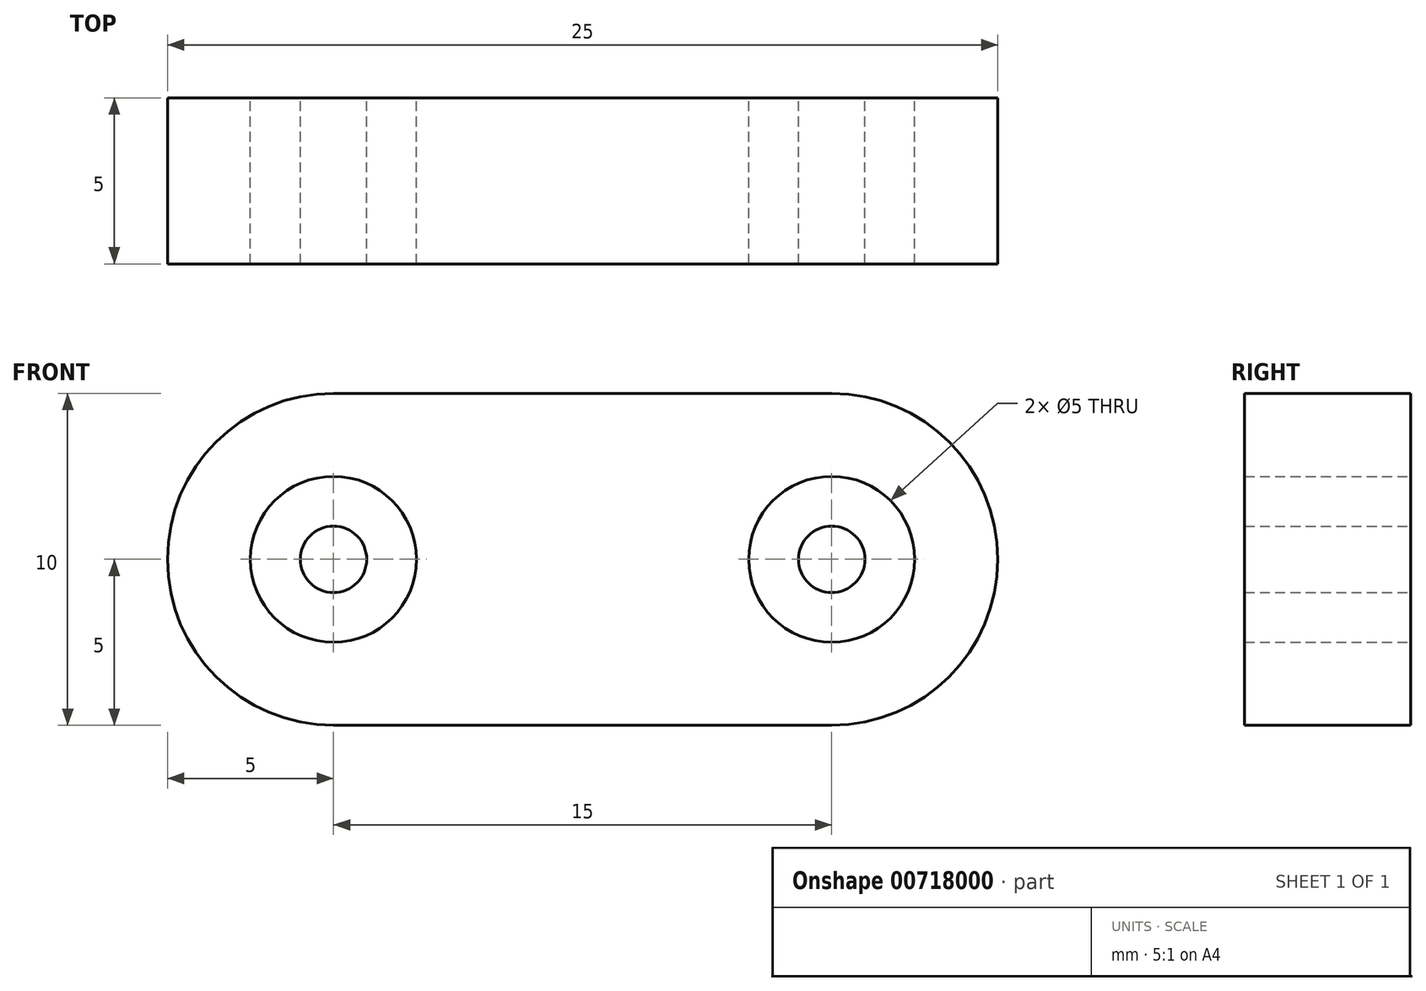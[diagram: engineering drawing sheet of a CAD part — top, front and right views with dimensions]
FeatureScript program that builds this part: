
annotation { "Feature Type Name" : "Feature", "Feature Type Description" : "" }
export const myFeature = defineFeature(function(context is Context, id is Id, definition is map)
    precondition{}
    {
        {
            var Q0;
            Q0=qCreatedBy(makeId("Front.planeOp"),FACE);
            var sketch = newSketch(context, id + "F0", { "sketchPlane" : qUnion([Q0])});
            skCircle(sketch, "E0", {"center": v(0, 0) * mm, "radius": 5 * mm});
            skCircle(sketch, "E1", {"center": v(15, 0) * mm, "radius": 5 * mm});
            skLineSegment(sketch, "E2", {"start": v(0, -5) * mm, "end": v(15, -5) * mm});
            skLineSegment(sketch, "E3", {"start": v(0, 5) * mm, "end": v(15, 5) * mm});
            skCircle(sketch, "E4", {"center": v(15, 0) * mm, "radius": 1 * mm});
            skCircle(sketch, "E5", {"center": v(15, 0) * mm, "radius": 2.5 * mm});
            skCircle(sketch, "E6", {"center": v(0, 0) * mm, "radius": 2.5 * mm});
            skCircle(sketch, "E7", {"center": v(0, 0) * mm, "radius": 1 * mm});
            skSolve(sketch);
        }
        {
            var Q0;
            Q0=makeQuery(id+"F0.imprint","IMPRINT",FACE,{"disambiguationData":[TD([[makeQuery(id+"F0.imprint","IMPRINT",EDGE,{"derivedFrom":sQuery(id+"F0.wireOp",EDGE,"E6")}),-1.0]])]});
            var Q1;
            Q1=makeQuery(id+"F0.imprint","IMPRINT",FACE,{"disambiguationData":[TD([[makeQuery(id+"F0.imprint","IMPRINT",EDGE,{"derivedFrom":sQuery(id+"F0.wireOp",EDGE,"E5")}),-1.0]])]});
            var Q2;
            {var subQ0=sQuery(id+"F0.wireOp",EDGE,"E2");Q2=makeQuery(id+"F0.imprint","IMPRINT",FACE,{"disambiguationData":[TD([[makeQuery(id+"F0.imprint","IMPRINT",EDGE,{"derivedFrom":subQ0}),1.0]])]});}
            var Q3;
            Q3=makeQuery(id+"F0.imprint","IMPRINT",FACE,{"disambiguationData":[TD([[makeQuery(id+"F0.imprint","IMPRINT",EDGE,{"derivedFrom":sQuery(id+"F0.wireOp",EDGE,"E7")}),1.0]])]});
            var Q4;
            Q4=makeQuery(id+"F0.imprint","IMPRINT",FACE,{"disambiguationData":[TD([[makeQuery(id+"F0.imprint","IMPRINT",EDGE,{"derivedFrom":sQuery(id+"F0.wireOp",EDGE,"E4")}),1.0]])]});
            extrude(context, id + "F1", {"entities" : qUnion([Q0, Q1, Q2, Q3, Q4]), "depth" : 5 * mm, "offsetDistance" : 25 * mm});
        }
    });
